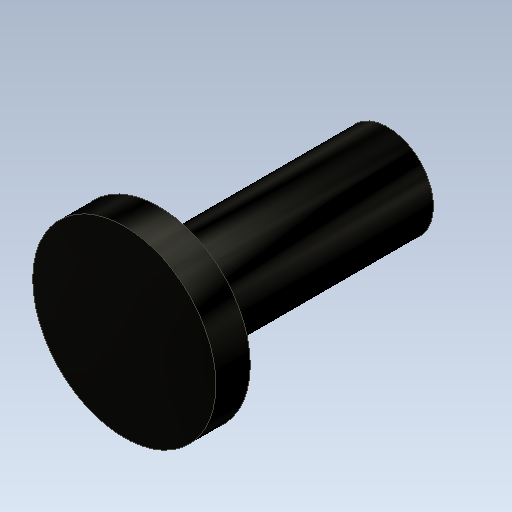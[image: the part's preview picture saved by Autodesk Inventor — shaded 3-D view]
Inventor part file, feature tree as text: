
AUTODESK INVENTOR PART (.ipt)
format: ipt  version: 2020.2 (Build 242310000, 310)  size: 104,960 bytes
history: native  units: mm
features: extrude x2, other x1, sketch x1
ambient origin geometry x8: Origin, YZ Plane, XZ Plane, XY Plane, X Axis, Y Axis, Z Axis, Center Point
bodies: Body1 (feature_tree)
feature tree (4):
  other  "ソリッド1"
  sketch  "スケッチ1"
  extrude  "押し出し1"  Depth=8.0mm
  extrude  "押し出し2"  Depth=4.0mm
